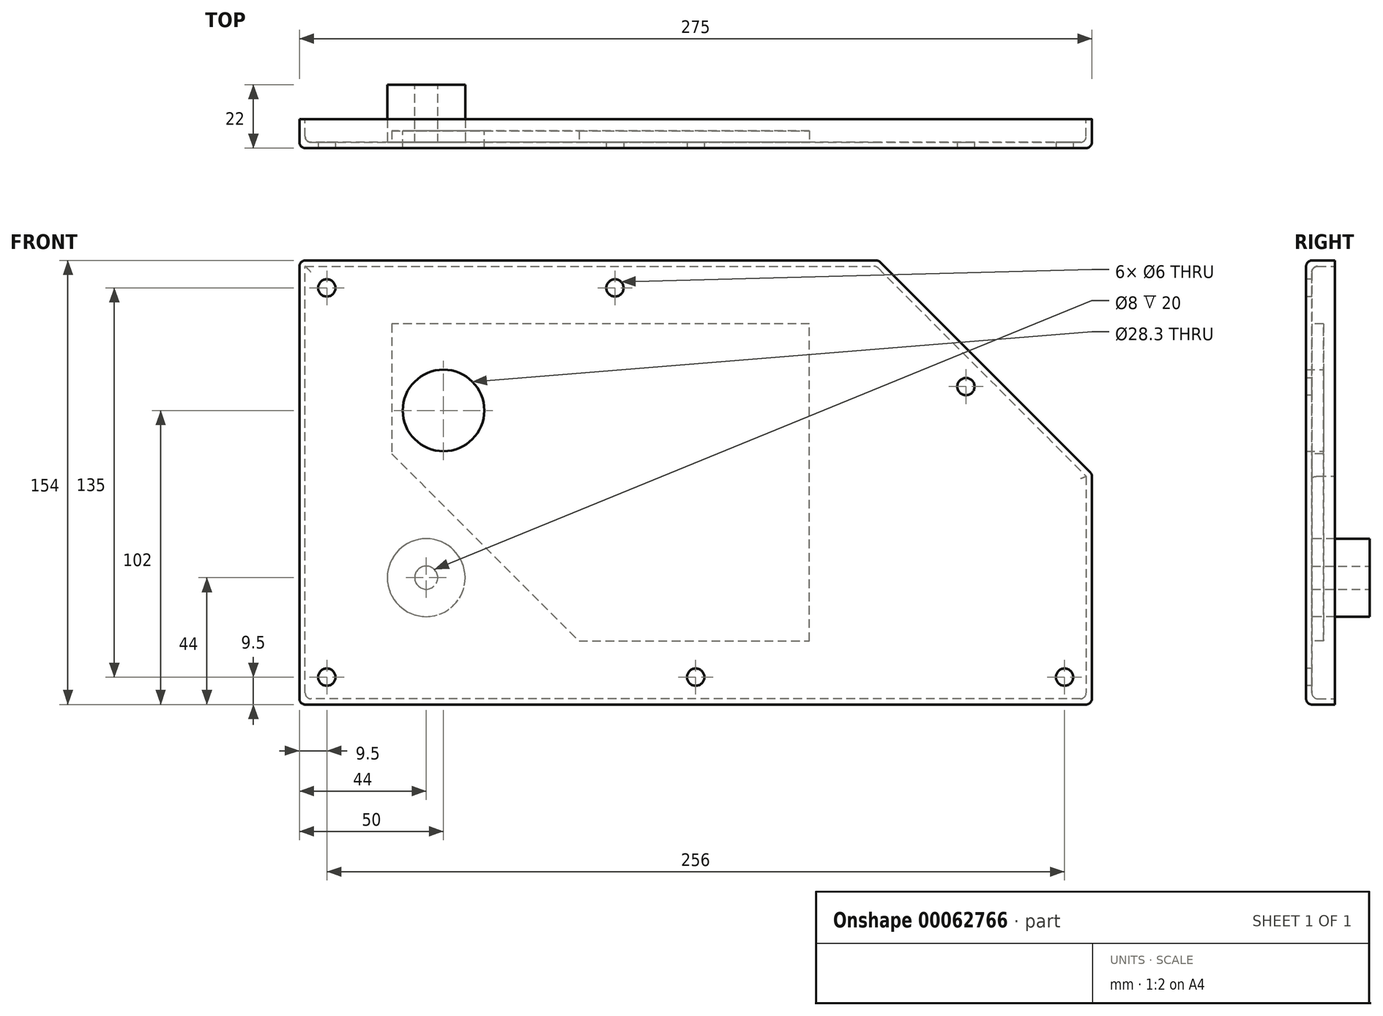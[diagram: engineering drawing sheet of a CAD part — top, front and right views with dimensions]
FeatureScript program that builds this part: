
annotation { "Feature Type Name" : "Feature", "Feature Type Description" : "" }
export const myFeature = defineFeature(function(context is Context, id is Id, definition is map)
    precondition{}
    {
        {
            var Q0;
            Q0=qCreatedBy(makeId("Front.planeOp"),FACE);
            var sketch = newSketch(context, id + "F0", { "sketchPlane" : qUnion([Q0])});
            skLineSegment(sketch, "E0", {"start": v(0, 0) * mm, "end": v(0, 154) * mm});
            skLineSegment(sketch, "E1", {"start": v(0, 154) * mm, "end": v(201, 154) * mm});
            skLineSegment(sketch, "E2", {"start": v(201, 154) * mm, "end": v(275, 80) * mm});
            skLineSegment(sketch, "E3", {"start": v(275, 80) * mm, "end": v(275, 0) * mm});
            skLineSegment(sketch, "E4", {"start": v(275, 0) * mm, "end": v(0, 0) * mm});
            skSolve(sketch);
        }
        {
            var Q0;
            Q0=makeQuery(id+"F0.imprint","IMPRINT",FACE,{"disambiguationData":[TD([[makeQuery(id+"F0.imprint","IMPRINT",EDGE,{"derivedFrom":sQuery(id+"F0.wireOp",EDGE,"E0")}),-1.0]])]});
            extrude(context, id + "F1", {"entities" : qUnion([Q0]), "depth" : 10 * mm});
        }
        {
            var Q0;
            Q0=makeQuery(id+"F1.opExtrude","CAP_FACE",FACE,{"disambiguationData":[OSD([sQuery(id+"F0.wireOp",EDGE,"E0"),sQuery(id+"F0.wireOp",EDGE,"E1"),sQuery(id+"F0.wireOp",EDGE,"E2"),sQuery(id+"F0.wireOp",EDGE,"E3"),sQuery(id+"F0.wireOp",EDGE,"E4")])],"isStart":true});
            shell(context, id + "F2", {"entities" : qUnion([Q0]), "thickness" : 2 * mm});
        }
        {
            var Q0;
            Q0=makeQuery(id+"F2.opShell","OFFSET_FACE",FACE,{"disambiguationData":[OSD([sQuery(id+"F0.wireOp",EDGE,"E0"),sQuery(id+"F0.wireOp",EDGE,"E1"),sQuery(id+"F0.wireOp",EDGE,"E2"),sQuery(id+"F0.wireOp",EDGE,"E3"),sQuery(id+"F0.wireOp",EDGE,"E4")])]});
            var sketch = newSketch(context, id + "F3", { "sketchPlane" : qUnion([Q0])});
            skLineSegment(sketch, "E5", {"start": v(-32, 132) * mm, "end": v(-32, 87) * mm});
            skLineSegment(sketch, "E6", {"start": v(-32, 87) * mm, "end": v(-97, 22) * mm});
            skLineSegment(sketch, "E7", {"start": v(-97, 22) * mm, "end": v(-177, 22) * mm});
            skLineSegment(sketch, "E8", {"start": v(-177, 22) * mm, "end": v(-177, 132) * mm});
            skLineSegment(sketch, "E9", {"start": v(-177, 132) * mm, "end": v(-32, 132) * mm});
            skSolve(sketch);
        }
        {
            var Q0;
            Q0=qSketchRegion(id+"F3",true);
            var Q1;
            Q1=makeQuery(id+"F3.imprint","IMPRINT",FACE,{"disambiguationData":[TD([[makeQuery(id+"F3.imprint","IMPRINT",EDGE,{"derivedFrom":sQuery(id+"F3.wireOp",EDGE,"E5")}),-1.0]])]});
            extrude(context, id + "F4", {"entities" : qUnion([Q0, Q1]), "operationType" : NewBodyOperationType.ADD, "depth" : 4 * mm});
        }
        {
            var Q0;
            Q0=makeQuery(id+"F2.opShell","OFFSET_FACE",FACE,{"disambiguationData":[OSD([sQuery(id+"F0.wireOp",EDGE,"E0"),sQuery(id+"F0.wireOp",EDGE,"E1"),sQuery(id+"F0.wireOp",EDGE,"E2"),sQuery(id+"F0.wireOp",EDGE,"E3"),sQuery(id+"F0.wireOp",EDGE,"E4")])]});
            var sketch = newSketch(context, id + "F5", { "sketchPlane" : qUnion([Q0])});
            skCircle(sketch, "E10", {"center": v(-44, 44) * mm, "radius": 13.5 * mm});
            skSolve(sketch);
        }
        {
            var Q0;
            Q0=qSketchRegion(id+"F5",true);
            extrude(context, id + "F6", {"entities" : qUnion([Q0]), "operationType" : NewBodyOperationType.ADD, "depth" : 20 * mm});
        }
        {
            var Q0;
            Q0=makeQuery(id+"F6.opExtrude","CAP_FACE",FACE,{"disambiguationData":[OSD([sQuery(id+"F5.wireOp",EDGE,"E10")])],"isStart":false});
            var sketch = newSketch(context, id + "F7", { "sketchPlane" : qUnion([Q0])});
            skPoint(sketch, "E11", {"position": v(-44, 44) * mm});
            skCircle(sketch, "E12", {"center": v(-44, 44) * mm, "radius": 4 * mm});
            skSolve(sketch);
        }
        {
            var Q0;
            Q0=makeQuery(id+"F7.imprint","IMPRINT",FACE,{"disambiguationData":[TD([[makeQuery(id+"F7.imprint","IMPRINT",EDGE,{"derivedFrom":sQuery(id+"F7.wireOp",EDGE,"E12")}),1.0]])]});
            var Q1;
            Q1=makeQuery(id+"F2.opShell","OFFSET_FACE",FACE,{"disambiguationData":[OSD([sQuery(id+"F0.wireOp",EDGE,"E0"),sQuery(id+"F0.wireOp",EDGE,"E1"),sQuery(id+"F0.wireOp",EDGE,"E2"),sQuery(id+"F0.wireOp",EDGE,"E3"),sQuery(id+"F0.wireOp",EDGE,"E4")])]});
            extrude(context, id + "F8", {"entities" : qUnion([Q0]), "operationType" : NewBodyOperationType.REMOVE, "endBound" : BoundingType.UP_TO_SURFACE, "oppositeDirection" : true, "endBoundEntityFace" : qUnion([Q1]), "depth" : 25 * mm});
        }
        {
            var Q0;
            Q0=makeQuery(id+"F1.opExtrude","CAP_FACE",FACE,{"disambiguationData":[OSD([sQuery(id+"F0.wireOp",EDGE,"E0"),sQuery(id+"F0.wireOp",EDGE,"E1"),sQuery(id+"F0.wireOp",EDGE,"E2"),sQuery(id+"F0.wireOp",EDGE,"E3"),sQuery(id+"F0.wireOp",EDGE,"E4")])],"isStart":false});
            var sketch = newSketch(context, id + "F9", { "sketchPlane" : qUnion([Q0])});
            skLineSegment(sketch, "E13.0", {"start": v(9.5, 9.5) * mm, "end": v(265.5, 9.5) * mm, "construction": true});
            skLineSegment(sketch, "E13.1", {"start": v(9.5, 144.5) * mm, "end": v(9.5, 9.5) * mm, "construction": true});
            skLineSegment(sketch, "E13.2", {"start": v(265.5, 9.5) * mm, "end": v(265.5, 76.06) * mm, "construction": true});
            skLineSegment(sketch, "E13.3", {"start": v(265.5, 76.06) * mm, "end": v(197.06, 144.5) * mm, "construction": true});
            skLineSegment(sketch, "E13.4", {"start": v(197.06, 144.5) * mm, "end": v(9.5, 144.5) * mm, "construction": true});
            skPoint(sketch, "E14", {"position": v(9.5, 144.5) * mm});
            skPoint(sketch, "E15", {"position": v(109.5, 144.5) * mm});
            skPoint(sketch, "E16", {"position": v(231.28, 110.28) * mm});
            skPoint(sketch, "E17", {"position": v(265.5, 9.5) * mm});
            skPoint(sketch, "E18", {"position": v(137.5, 9.5) * mm});
            skPoint(sketch, "E19", {"position": v(9.5, 9.5) * mm});
            skSolve(sketch);
        }
        {
            var Q0;
            Q0=sQuery(id+"F9.wireOp",VERTEX,"E14");
            var Q1;
            Q1=sQuery(id+"F9.wireOp",VERTEX,"E15");
            var Q2;
            Q2=sQuery(id+"F9.wireOp",VERTEX,"E16");
            var Q3;
            Q3=sQuery(id+"F9.wireOp",VERTEX,"E17");
            var Q4;
            Q4=sQuery(id+"F9.wireOp",VERTEX,"E18");
            var Q5;
            Q5=sQuery(id+"F9.wireOp",VERTEX,"E19");
            var Q6;
            Q6=makeQuery(id+"F1.opExtrude","SWEPT_BODY",BODY,{"disambiguationData":[OSD([sQuery(id+"F0.wireOp",EDGE,"E0"),sQuery(id+"F0.wireOp",EDGE,"E1"),sQuery(id+"F0.wireOp",EDGE,"E2"),sQuery(id+"F0.wireOp",EDGE,"E3"),sQuery(id+"F0.wireOp",EDGE,"E4")])]});
            hole(context, id + "F10", {"style" : HoleStyle.SIMPLE, "holeDiameter" : 6 * mm, "endStyle" : HoleEndStyle.THROUGH, "locations" : qUnion([Q0, Q1, Q2, Q3, Q4, Q5]), "scope" : qUnion([Q6])});
        }
        {
            var Q0;
            Q0=makeQuery(id+"F1.opExtrude","CAP_EDGE",EDGE,{"disambiguationData":[OSD([sQuery(id+"F0.wireOp",EDGE,"E0")])],"isStart":false});
            var Q1;
            Q1=makeQuery(id+"F1.opExtrude","CAP_EDGE",EDGE,{"disambiguationData":[OSD([sQuery(id+"F0.wireOp",EDGE,"E4")])],"isStart":false});
            var Q2;
            Q2=makeQuery(id+"F1.opExtrude","CAP_EDGE",EDGE,{"disambiguationData":[OSD([sQuery(id+"F0.wireOp",EDGE,"E2")])],"isStart":false});
            var Q3;
            Q3=makeQuery(id+"F1.opExtrude","CAP_EDGE",EDGE,{"disambiguationData":[OSD([sQuery(id+"F0.wireOp",EDGE,"E3")])],"isStart":false});
            var Q4;
            Q4=makeQuery(id+"F1.opExtrude","SWEPT_EDGE",EDGE,{"disambiguationData":[OSD([sQuery(id+"F0.wireOp",EDGE,"E3"),sQuery(id+"F0.wireOp",EDGE,"E4")])]});
            var Q5;
            Q5=makeQuery(id+"F1.opExtrude","SWEPT_EDGE",EDGE,{"disambiguationData":[OSD([sQuery(id+"F0.wireOp",EDGE,"E2"),sQuery(id+"F0.wireOp",EDGE,"E3")])]});
            var Q6;
            Q6=makeQuery(id+"F1.opExtrude","SWEPT_EDGE",EDGE,{"disambiguationData":[OSD([sQuery(id+"F0.wireOp",EDGE,"E1"),sQuery(id+"F0.wireOp",EDGE,"E2")])]});
            var Q7;
            Q7=makeQuery(id+"F1.opExtrude","SWEPT_EDGE",EDGE,{"disambiguationData":[OSD([sQuery(id+"F0.wireOp",EDGE,"E0"),sQuery(id+"F0.wireOp",EDGE,"E4")])]});
            var Q8;
            Q8=makeQuery(id+"F1.opExtrude","CAP_EDGE",EDGE,{"disambiguationData":[OSD([sQuery(id+"F0.wireOp",EDGE,"E1")])],"isStart":false});
            var Q9;
            Q9=makeQuery(id+"F1.opExtrude","SWEPT_EDGE",EDGE,{"disambiguationData":[OSD([sQuery(id+"F0.wireOp",EDGE,"E0"),sQuery(id+"F0.wireOp",EDGE,"E1")])]});
            fillet(context, id + "F11", {"entities" : qUnion([Q0, Q1, Q2, Q3, Q4, Q5, Q6, Q7, Q8, Q9]), "radius" : 2 * mm, "tangentPropagation" : true, "allowEdgeOverflow" : false});
        }
        {
            var Q0;
            Q0=makeQuery(id+"F2.opShell","OFFSET_EDGE",EDGE,{"disambiguationData":[OSD([sQuery(id+"F0.wireOp",EDGE,"E3"),sQuery(id+"F0.wireOp",EDGE,"E4")])]});
            var Q1;
            {var subQ0=sQuery(id+"F0.wireOp",EDGE,"E4");Q1=makeQuery(id+"F2.opShell","OFFSET_EDGE",EDGE,{"disambiguationData":[OSD([subQ0]),TDD([makeQuery(id+"F1.opExtrude","CAP_EDGE",EDGE,{"disambiguationData":[OSD([subQ0])],"isStart":false})])]});}
            var Q2;
            {var subQ0=sQuery(id+"F0.wireOp",EDGE,"E3");Q2=makeQuery(id+"F2.opShell","OFFSET_EDGE",EDGE,{"disambiguationData":[OSD([subQ0]),TDD([makeQuery(id+"F1.opExtrude","CAP_EDGE",EDGE,{"disambiguationData":[OSD([subQ0])],"isStart":false})])]});}
            var Q3;
            {var subQ0=sQuery(id+"F0.wireOp",EDGE,"E2");Q3=makeQuery(id+"F2.opShell","OFFSET_EDGE",EDGE,{"disambiguationData":[OSD([subQ0]),TDD([makeQuery(id+"F1.opExtrude","CAP_EDGE",EDGE,{"disambiguationData":[OSD([subQ0])],"isStart":false})])]});}
            var Q4;
            Q4=makeQuery(id+"F2.opShell","OFFSET_EDGE",EDGE,{"disambiguationData":[OSD([sQuery(id+"F0.wireOp",EDGE,"E1"),sQuery(id+"F0.wireOp",EDGE,"E2")])]});
            var Q5;
            {var subQ0=sQuery(id+"F0.wireOp",EDGE,"E1");Q5=makeQuery(id+"F2.opShell","OFFSET_EDGE",EDGE,{"disambiguationData":[OSD([subQ0]),TDD([makeQuery(id+"F1.opExtrude","CAP_EDGE",EDGE,{"disambiguationData":[OSD([subQ0])],"isStart":false})])]});}
            var Q6;
            Q6=makeQuery(id+"F2.opShell","OFFSET_EDGE",EDGE,{"disambiguationData":[OSD([sQuery(id+"F0.wireOp",EDGE,"E0"),sQuery(id+"F0.wireOp",EDGE,"E4")])]});
            var Q7;
            {var subQ0=sQuery(id+"F0.wireOp",EDGE,"E0");Q7=makeQuery(id+"F2.opShell","OFFSET_EDGE",EDGE,{"disambiguationData":[OSD([subQ0]),TDD([makeQuery(id+"F1.opExtrude","CAP_EDGE",EDGE,{"disambiguationData":[OSD([subQ0])],"isStart":false})])]});}
            fillet(context, id + "F12", {"entities" : qUnion([Q0, Q1, Q2, Q3, Q4, Q5, Q6, Q7]), "radius" : 2 * mm, "tangentPropagation" : true, "allowEdgeOverflow" : false});
        }
        {
            var Q0;
            Q0=makeQuery(id+"F4.opExtrude","CAP_FACE",FACE,{"disambiguationData":[OSD([sQuery(id+"F3.wireOp",EDGE,"E5"),sQuery(id+"F3.wireOp",EDGE,"E6"),sQuery(id+"F3.wireOp",EDGE,"E7"),sQuery(id+"F3.wireOp",EDGE,"E8"),sQuery(id+"F3.wireOp",EDGE,"E9")])],"isStart":false});
            var sketch = newSketch(context, id + "F13", { "sketchPlane" : qUnion([Q0])});
            skCircle(sketch, "E20", {"center": v(-50, 102) * mm, "radius": 14.15 * mm});
            skSolve(sketch);
        }
        {
            var Q0;
            Q0=qSketchRegion(id+"F13",true);
            extrude(context, id + "F14", {"entities" : qUnion([Q0]), "operationType" : NewBodyOperationType.REMOVE, "endBound" : BoundingType.THROUGH_ALL, "oppositeDirection" : true, "depth" : 25 * mm});
        }
    });
